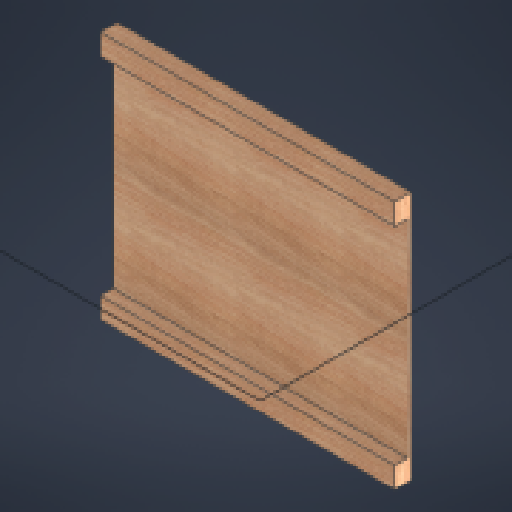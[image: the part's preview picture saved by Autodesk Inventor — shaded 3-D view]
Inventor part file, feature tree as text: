
AUTODESK INVENTOR PART (.ipt)
format: ipt  version: 2023.2 (Build 272271030, 271C)  size: 454,144 bytes
history: native  units: mm
features: extrude x1, sketch x1
ambient origin geometry x8: Origin, YZ Plane, XZ Plane, XY Plane, X Axis, Y Axis, Z Axis, Center Point
bodies: Volumenkörper1 (feature_tree)
feature tree (2):
  extrude  "Extrusion1"  Depth=30.0mm
  sketch  "Skizze1"  dims[d0=50.0mm d1=30.0mm d2=600.0mm d3=10.0mm d4=700.0mm d5=0.0mm]
